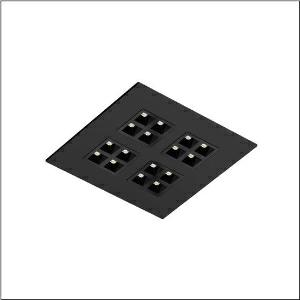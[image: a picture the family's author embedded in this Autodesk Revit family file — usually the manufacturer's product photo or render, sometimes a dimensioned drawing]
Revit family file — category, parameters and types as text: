
# Revit family: silica_31_square_51my6lms34ba
name_source: partatom
category: Lighting Fixtures
units: mm (PartAtom-declared; Revit-internal decimal feet)

## family parameters
Cut with Voids When Loaded = No
Host = Face
Light Source = No
Part Type = Normal
Room Calculation Point = No
Round Connector Dimension = Use Diameter
Shared = No

## types (1)
- --- (1 x LED, 6250 lm, 39 W, 3000K)
    Apparent Load = 39 VA
    CIE Flux Codes = 82 100 100 100 100
    Color Rendering = 80
    Color Temperature = 3000K
    Default Elevation = 1800 mm
    Description = Silica 31 Square, office luminaire, primary light control with lens, of PMMA, primary anti-glare with reflector, of PC, black, light emission: direct distribution, primary light characteristic: symmetric, installation type: lay-in mounting, LED, rated luminous flux: 4.600lm, luminous efficacy: 166lm/W, light colour: 830, colour temperature: 3000K, control gear: ON/OFF Multilumen, with terminal, 3-pole, mains connection: 220..240V, AC, 50/60Hz, rated input power: 27.7W, luminaire housing, of sheet steel, coated, jet black (RAL 9005), module: M600, length: 595mm, width: 595mm, height: 43mm, protection rating (complete): IP20, insulation class (complete): insulation class II (safety insulation), certification: CE, impact resistance: IK03, permissible operating ambient temperature: -20..+35°C, standard: EN 50419, packaging unit: 1 piece
    Height = 0 mm  [stored 0 ft]
    Lamp = 1 x LED
    Lamp Light Flux = 6250 lm
    Lamp Power = 39 W
    Lamp count = 1
    Length = 595 mm
    Luminous efficacy = 160 lm/W
    Manufacturer = Siteco
    ModVariant = No
    Model = 51MY6LMS34BA
    Mounting Place = Ceiling
    Mounting Type = Recessed
    Number of Poles = 1
    OnlyDefault = Yes
    Power Factor = 1
    Product Name = Silica 31 Square
    Product group = office luminaire | ceiling recessed
    ProductGroupID = 400
    Protection Class = Protection class II
    Protection Degree = IP 20
    RLX_Detail_Level = 1
    RLX_Emergency_Light_Flux = 0 lm
    RLX_Emergency_Type = 0
    RLX_Emergency_Type_DB = No
    RlxData = <blob elided: 36105 chars, md5=1b605bee>
    Socket = socket
    Standby Power = 0 W
    System Light Flux = 6250 lm
    System Power = 39 W
    Type Comments = factory setting: luminous flux: 100 % | (ON | ON | ON | ON) | 1100 mA
    Type Image = l_1313660.jpg
    URL = http://relux.com
    VarID = @adj_044765
    Voltage = 0 V
    Weight = 0.00 kg
    Width = 595 mm

note: [stored X ft] marks values corroborated as IEEE doubles in the binary element streams (Revit-internal decimal feet)

## geometry (parser evidence)
native form markers: Blend x4, Sweep x10
no freeform markers — native parametric forms only
